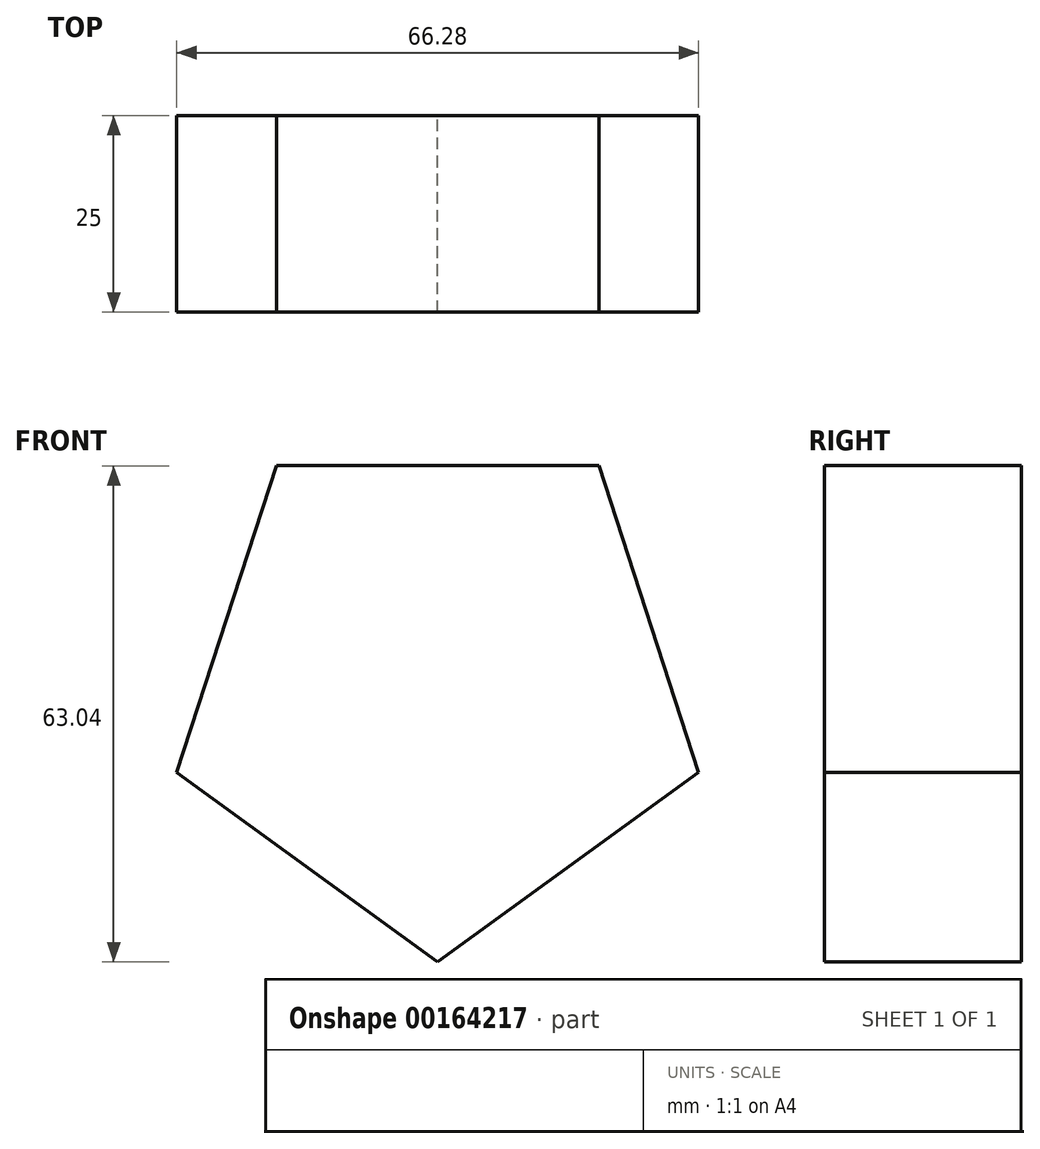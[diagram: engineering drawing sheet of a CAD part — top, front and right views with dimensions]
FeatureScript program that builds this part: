
annotation { "Feature Type Name" : "Feature", "Feature Type Description" : "" }
export const myFeature = defineFeature(function(context is Context, id is Id, definition is map)
    precondition{}
    {
        {
            var Q0;
            Q0=qCreatedBy(makeId("Front.planeOp"),FACE);
            var sketch = newSketch(context, id + "F0", { "sketchPlane" : qUnion([Q0])});
            skCircle(sketch, "E0.cCircle", {"center": v(0, 0) * mm, "radius": 28.2 * mm, "construction": true});
            skLineSegment(sketch, "E0.0", {"start": v(33.14, -10.77) * mm, "end": v(0, -34.85) * mm});
            skLineSegment(sketch, "E0.1", {"start": v(0, -34.85) * mm, "end": v(-33.14, -10.77) * mm});
            skLineSegment(sketch, "E0.2", {"start": v(-33.14, -10.77) * mm, "end": v(-20.48, 28.2) * mm});
            skLineSegment(sketch, "E0.3", {"start": v(-20.48, 28.2) * mm, "end": v(20.48, 28.2) * mm});
            skLineSegment(sketch, "E0.4", {"start": v(20.48, 28.2) * mm, "end": v(33.14, -10.77) * mm});
            skPoint(sketch, "E0.0.midPoint", {"position": v(16.57, -22.8) * mm});
            skSolve(sketch);
        }
        {
            var Q0;
            Q0=makeQuery(id+"F0.imprint","IMPRINT",FACE,{"disambiguationData":[TD([[makeQuery(id+"F0.imprint","IMPRINT",EDGE,{"derivedFrom":sQuery(id+"F0.wireOp",EDGE,"E0.0")}),-1.0]])]});
            extrude(context, id + "F1", {"entities" : qUnion([Q0]), "depth" : 25 * mm});
        }
    });
